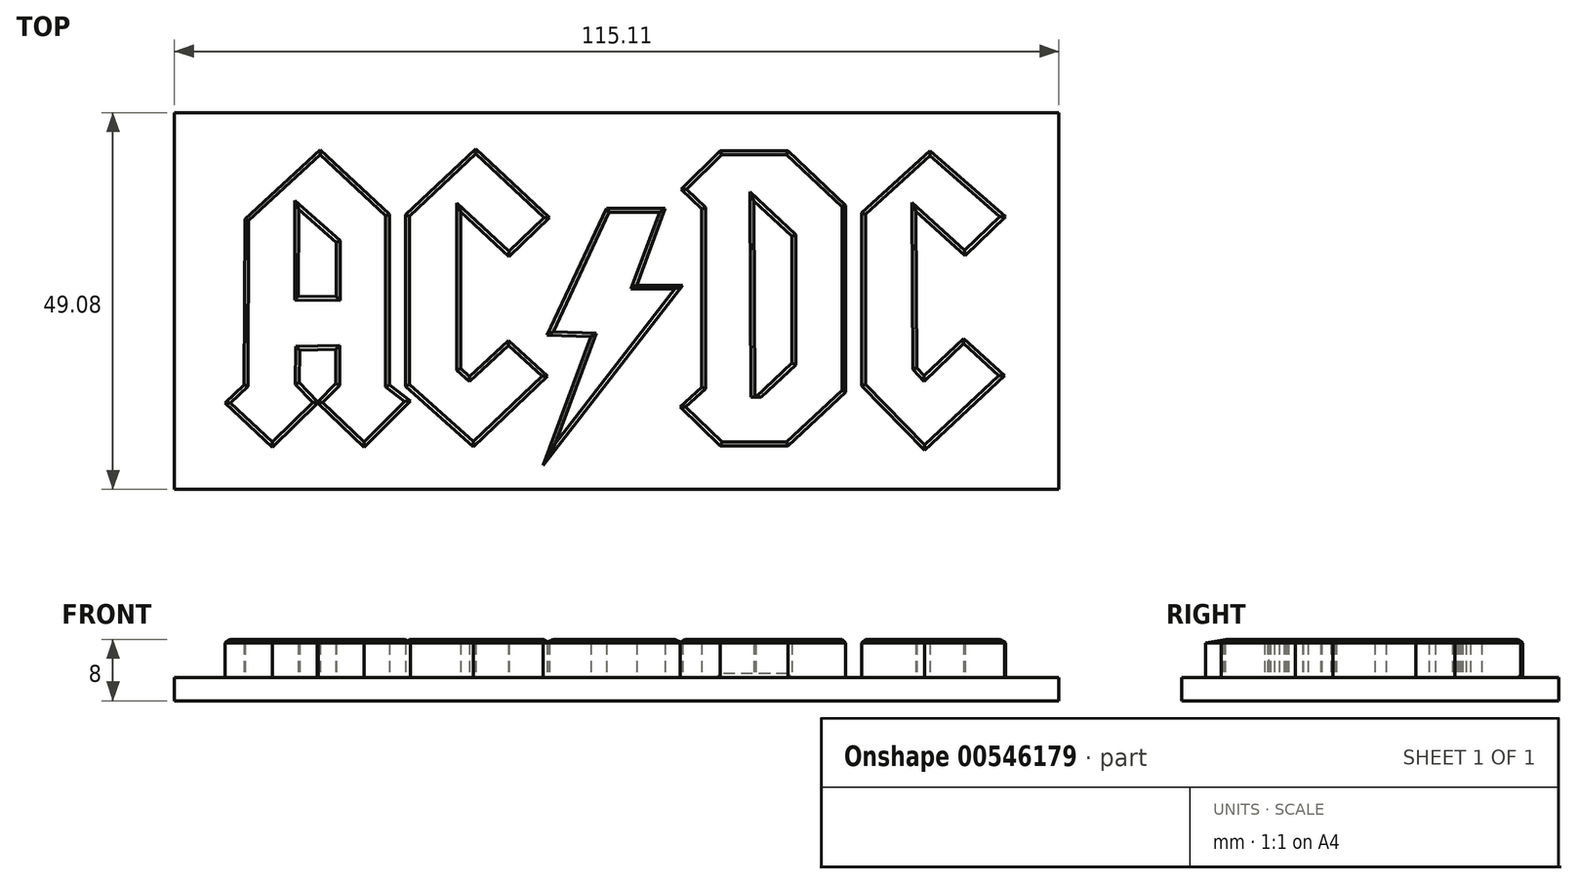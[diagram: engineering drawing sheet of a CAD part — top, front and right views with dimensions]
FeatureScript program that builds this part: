
annotation { "Feature Type Name" : "Feature", "Feature Type Description" : "" }
export const myFeature = defineFeature(function(context is Context, id is Id, definition is map)
    precondition{}
    {
        {
            var Q0;
            Q0=qCreatedBy(makeId("Top.planeOp"),FACE);
            var sketch = newSketch(context, id + "F0", { "sketchPlane" : qUnion([Q0])});
            skLineSegment(sketch, "E0", {"start": v(-47.24, 13.54) * mm, "end": v(-37.43, 22.56) * mm});
            skLineSegment(sketch, "E1", {"start": v(-37.43, 22.56) * mm, "end": v(-28.4, 14.16) * mm});
            skLineSegment(sketch, "E2", {"start": v(-28.4, 14.16) * mm, "end": v(-28.4, -8.08) * mm});
            skLineSegment(sketch, "E3", {"start": v(-49.82, -10.4) * mm, "end": v(-47.34, -8.08) * mm});
            skLineSegment(sketch, "E4", {"start": v(-47.34, -8.08) * mm, "end": v(-47.24, 13.54) * mm});
            skLineSegment(sketch, "E5", {"start": v(-40.2, 14.8) * mm, "end": v(-40.26, 3.45) * mm});
            skLineSegment(sketch, "E6", {"start": v(-40.26, 3.45) * mm, "end": v(-35.34, 3.43) * mm});
            skLineSegment(sketch, "E7", {"start": v(-35.34, 3.43) * mm, "end": v(-35.34, 10.49) * mm});
            skLineSegment(sketch, "E8", {"start": v(-35.34, 10.49) * mm, "end": v(-40.2, 14.8) * mm});
            skLineSegment(sketch, "E9", {"start": v(-40.1, -3.57) * mm, "end": v(-35.37, -3.46) * mm});
            skLineSegment(sketch, "E10", {"start": v(-35.37, -3.46) * mm, "end": v(-35.37, -7.9) * mm});
            skLineSegment(sketch, "E11", {"start": v(-40.18, -7.78) * mm, "end": v(-37.8, -10.25) * mm});
            skLineSegment(sketch, "E12", {"start": v(-40.18, -7.78) * mm, "end": v(-40.1, -3.57) * mm});
            skLineSegment(sketch, "E13", {"start": v(-28.4, -8.08) * mm, "end": v(-25.7, -10.15) * mm});
            skLineSegment(sketch, "E14", {"start": v(-25.7, -10.15) * mm, "end": v(-31.7, -16.22) * mm});
            skLineSegment(sketch, "E15", {"start": v(-31.7, -16.22) * mm, "end": v(-37.7, -10.5) * mm});
            skLineSegment(sketch, "E16", {"start": v(-37.7, -10.5) * mm, "end": v(-37.63, -10.41) * mm});
            skLineSegment(sketch, "E17", {"start": v(-37.63, -10.41) * mm, "end": v(-37.72, -10.28) * mm});
            skLineSegment(sketch, "E18", {"start": v(-37.72, -10.28) * mm, "end": v(-35.37, -7.9) * mm});
            skLineSegment(sketch, "E19", {"start": v(-37.8, -10.25) * mm, "end": v(-37.89, -10.38) * mm});
            skLineSegment(sketch, "E20", {"start": v(-37.89, -10.38) * mm, "end": v(-37.8, -10.5) * mm});
            skLineSegment(sketch, "E21", {"start": v(-37.8, -10.5) * mm, "end": v(-43.67, -16.18) * mm});
            skLineSegment(sketch, "E22", {"start": v(-43.67, -16.18) * mm, "end": v(-49.82, -10.4) * mm});
            skLineSegment(sketch, "E23", {"start": v(-12.87, 8.66) * mm, "end": v(-7.58, 13.71) * mm});
            skLineSegment(sketch, "E24", {"start": v(-7.58, 13.71) * mm, "end": v(-17.16, 22.69) * mm});
            skLineSegment(sketch, "E25", {"start": v(-17.16, 22.69) * mm, "end": v(-26.3, 14.11) * mm});
            skLineSegment(sketch, "E26", {"start": v(-26.3, 14.11) * mm, "end": v(-26.3, -8.25) * mm});
            skLineSegment(sketch, "E27", {"start": v(-26.3, -8.25) * mm, "end": v(-17.48, -16.14) * mm});
            skLineSegment(sketch, "E28", {"start": v(-17.48, -16.14) * mm, "end": v(-7.82, -6.93) * mm});
            skLineSegment(sketch, "E29", {"start": v(-7.82, -6.93) * mm, "end": v(-12.9, -2.28) * mm});
            skLineSegment(sketch, "E30", {"start": v(-12.9, -2.28) * mm, "end": v(-17.99, -6.96) * mm});
            skLineSegment(sketch, "E31", {"start": v(-17.99, -6.96) * mm, "end": v(-19.16, -5.93) * mm});
            skLineSegment(sketch, "E32", {"start": v(-19.16, -5.93) * mm, "end": v(-19.16, 14.47) * mm});
            skLineSegment(sketch, "E33", {"start": v(-19.16, 14.47) * mm, "end": v(-12.87, 8.66) * mm});
            skLineSegment(sketch, "E34", {"start": v(7.47, 14.9) * mm, "end": v(-0.15, 14.9) * mm});
            skLineSegment(sketch, "E35", {"start": v(-0.15, 14.9) * mm, "end": v(-7.88, -1.6) * mm});
            skLineSegment(sketch, "E36", {"start": v(-7.88, -1.6) * mm, "end": v(-2.18, -1.81) * mm});
            skLineSegment(sketch, "E37", {"start": v(-2.18, -1.81) * mm, "end": v(-8.4, -18.57) * mm});
            skLineSegment(sketch, "E38", {"start": v(-8.4, -18.57) * mm, "end": v(9.75, 4.9) * mm});
            skLineSegment(sketch, "E39", {"start": v(9.75, 4.9) * mm, "end": v(3.77, 4.9) * mm});
            skLineSegment(sketch, "E40", {"start": v(3.77, 4.9) * mm, "end": v(7.47, 14.9) * mm});
            skLineSegment(sketch, "E41", {"start": v(14.62, 22.43) * mm, "end": v(23.45, 22.43) * mm});
            skLineSegment(sketch, "E42", {"start": v(23.45, 22.43) * mm, "end": v(30.98, 15.31) * mm});
            skLineSegment(sketch, "E43", {"start": v(30.98, 15.31) * mm, "end": v(30.98, -9) * mm});
            skLineSegment(sketch, "E44", {"start": v(30.98, -9) * mm, "end": v(23.45, -16.03) * mm});
            skLineSegment(sketch, "E45", {"start": v(23.45, -16.03) * mm, "end": v(14.67, -16.03) * mm});
            skLineSegment(sketch, "E46", {"start": v(14.67, -16.03) * mm, "end": v(9.4, -10.93) * mm});
            skLineSegment(sketch, "E47", {"start": v(9.4, -10.93) * mm, "end": v(12.21, -8.37) * mm});
            skLineSegment(sketch, "E48", {"start": v(12.21, -8.37) * mm, "end": v(12.21, 14.84) * mm});
            skLineSegment(sketch, "E49", {"start": v(12.21, 14.84) * mm, "end": v(9.53, 17.37) * mm});
            skLineSegment(sketch, "E50", {"start": v(9.53, 17.37) * mm, "end": v(14.62, 22.43) * mm});
            skLineSegment(sketch, "E51", {"start": v(19.04, 15.9) * mm, "end": v(23.97, 11.3) * mm});
            skLineSegment(sketch, "E52", {"start": v(23.97, 11.3) * mm, "end": v(23.97, -5.23) * mm});
            skLineSegment(sketch, "E53", {"start": v(23.97, -5.23) * mm, "end": v(19.25, -9.66) * mm});
            skLineSegment(sketch, "E54", {"start": v(19.25, -9.66) * mm, "end": v(19.16, -9.66) * mm});
            skLineSegment(sketch, "E55", {"start": v(19.16, -9.66) * mm, "end": v(19.04, 15.9) * mm});
            skLineSegment(sketch, "E56", {"start": v(51.77, 13.84) * mm, "end": v(41.96, 22.43) * mm});
            skLineSegment(sketch, "E57", {"start": v(41.96, 22.43) * mm, "end": v(33.05, 14.35) * mm});
            skLineSegment(sketch, "E58", {"start": v(33.05, 14.35) * mm, "end": v(33.05, -8.2) * mm});
            skLineSegment(sketch, "E59", {"start": v(33.05, -8.2) * mm, "end": v(41.26, -16.56) * mm});
            skLineSegment(sketch, "E60", {"start": v(41.26, -16.56) * mm, "end": v(51.64, -6.9) * mm});
            skLineSegment(sketch, "E61", {"start": v(51.64, -6.9) * mm, "end": v(46.32, -2.02) * mm});
            skLineSegment(sketch, "E62", {"start": v(46.32, -2.02) * mm, "end": v(41.17, -6.9) * mm});
            skLineSegment(sketch, "E63", {"start": v(41.17, -6.9) * mm, "end": v(40.2, -5.87) * mm});
            skLineSegment(sketch, "E64", {"start": v(40.2, -5.87) * mm, "end": v(40.1, 14.55) * mm});
            skLineSegment(sketch, "E65", {"start": v(40.1, 14.55) * mm, "end": v(46.5, 8.78) * mm});
            skLineSegment(sketch, "E66", {"start": v(46.5, 8.78) * mm, "end": v(51.77, 13.84) * mm});
            skSolve(sketch);
        }
        {
            var Q0;
            Q0 = qSketchRegion(id + "F0", true);
            extrude(context, id + "F1", {"entities" : qUnion([Q0]), "depth" : 5 * mm, "offsetDistance" : 25.4 * mm});
        }
        {
            var Q0;
            Q0=makeQuery(id+"F1.opExtrude","CAP_EDGE",EDGE,{"disambiguationData":[OSD([sQuery(id+"F0.wireOp",EDGE,"E25")])],"isStart":false});
            var Q1;
            Q1=makeQuery(id+"F1.opExtrude","CAP_EDGE",EDGE,{"disambiguationData":[OSD([sQuery(id+"F0.wireOp",EDGE,"E24")])],"isStart":false});
            var Q2;
            Q2=makeQuery(id+"F1.opExtrude","CAP_EDGE",EDGE,{"disambiguationData":[OSD([sQuery(id+"F0.wireOp",EDGE,"E23")])],"isStart":false});
            var Q3;
            Q3=makeQuery(id+"F1.opExtrude","CAP_EDGE",EDGE,{"disambiguationData":[OSD([sQuery(id+"F0.wireOp",EDGE,"E33")])],"isStart":false});
            var Q4;
            Q4=makeQuery(id+"F1.opExtrude","CAP_EDGE",EDGE,{"disambiguationData":[OSD([sQuery(id+"F0.wireOp",EDGE,"E32")])],"isStart":false});
            var Q5;
            Q5=makeQuery(id+"F1.opExtrude","CAP_EDGE",EDGE,{"disambiguationData":[OSD([sQuery(id+"F0.wireOp",EDGE,"E31")])],"isStart":false});
            var Q6;
            Q6=makeQuery(id+"F1.opExtrude","CAP_EDGE",EDGE,{"disambiguationData":[OSD([sQuery(id+"F0.wireOp",EDGE,"E30")])],"isStart":false});
            var Q7;
            Q7=makeQuery(id+"F1.opExtrude","CAP_EDGE",EDGE,{"disambiguationData":[OSD([sQuery(id+"F0.wireOp",EDGE,"E29")])],"isStart":false});
            var Q8;
            Q8=makeQuery(id+"F1.opExtrude","CAP_EDGE",EDGE,{"disambiguationData":[OSD([sQuery(id+"F0.wireOp",EDGE,"E28")])],"isStart":false});
            var Q9;
            Q9=makeQuery(id+"F1.opExtrude","CAP_EDGE",EDGE,{"disambiguationData":[OSD([sQuery(id+"F0.wireOp",EDGE,"E27")])],"isStart":false});
            var Q10;
            Q10=makeQuery(id+"F1.opExtrude","CAP_EDGE",EDGE,{"disambiguationData":[OSD([sQuery(id+"F0.wireOp",EDGE,"E26")])],"isStart":false});
            chamfer(context, id + "F2", {"entities" : qUnion([Q0, Q1, Q2, Q3, Q4, Q5, Q6, Q7, Q8, Q9, Q10]), "width" : 0.5 * mm, "tangentPropagation" : true});
        }
        {
            var Q0;
            Q0=makeQuery(id+"F1.opExtrude","CAP_EDGE",EDGE,{"disambiguationData":[OSD([sQuery(id+"F0.wireOp",EDGE,"E0")])],"isStart":false});
            var Q1;
            Q1=makeQuery(id+"F1.opExtrude","CAP_EDGE",EDGE,{"disambiguationData":[OSD([sQuery(id+"F0.wireOp",EDGE,"E1")])],"isStart":false});
            var Q2;
            Q2=makeQuery(id+"F1.opExtrude","CAP_EDGE",EDGE,{"disambiguationData":[OSD([sQuery(id+"F0.wireOp",EDGE,"E2")])],"isStart":false});
            var Q3;
            Q3=makeQuery(id+"F1.opExtrude","CAP_EDGE",EDGE,{"disambiguationData":[OSD([sQuery(id+"F0.wireOp",EDGE,"E13")])],"isStart":false});
            var Q4;
            Q4=makeQuery(id+"F1.opExtrude","CAP_EDGE",EDGE,{"disambiguationData":[OSD([sQuery(id+"F0.wireOp",EDGE,"E14")])],"isStart":false});
            var Q5;
            Q5=makeQuery(id+"F1.opExtrude","CAP_EDGE",EDGE,{"disambiguationData":[OSD([sQuery(id+"F0.wireOp",EDGE,"E15")])],"isStart":false});
            var Q6;
            Q6=makeQuery(id+"F1.opExtrude","CAP_EDGE",EDGE,{"disambiguationData":[OSD([sQuery(id+"F0.wireOp",EDGE,"E4")])],"isStart":false});
            var Q7;
            Q7=makeQuery(id+"F1.opExtrude","CAP_EDGE",EDGE,{"disambiguationData":[OSD([sQuery(id+"F0.wireOp",EDGE,"E3")])],"isStart":false});
            var Q8;
            Q8=makeQuery(id+"F1.opExtrude","CAP_EDGE",EDGE,{"disambiguationData":[OSD([sQuery(id+"F0.wireOp",EDGE,"E22")])],"isStart":false});
            var Q9;
            Q9=makeQuery(id+"F1.opExtrude","CAP_EDGE",EDGE,{"disambiguationData":[OSD([sQuery(id+"F0.wireOp",EDGE,"E21")])],"isStart":false});
            var Q10;
            Q10=makeQuery(id+"F1.opExtrude","CAP_EDGE",EDGE,{"disambiguationData":[OSD([sQuery(id+"F0.wireOp",EDGE,"E11")])],"isStart":false});
            var Q11;
            Q11=makeQuery(id+"F1.opExtrude","CAP_EDGE",EDGE,{"disambiguationData":[OSD([sQuery(id+"F0.wireOp",EDGE,"E12")])],"isStart":false});
            var Q12;
            Q12=makeQuery(id+"F1.opExtrude","CAP_EDGE",EDGE,{"disambiguationData":[OSD([sQuery(id+"F0.wireOp",EDGE,"E9")])],"isStart":false});
            var Q13;
            Q13=makeQuery(id+"F1.opExtrude","CAP_EDGE",EDGE,{"disambiguationData":[OSD([sQuery(id+"F0.wireOp",EDGE,"E10")])],"isStart":false});
            var Q14;
            Q14=makeQuery(id+"F1.opExtrude","CAP_EDGE",EDGE,{"disambiguationData":[OSD([sQuery(id+"F0.wireOp",EDGE,"E18")])],"isStart":false});
            var Q15;
            Q15=makeQuery(id+"F1.opExtrude","CAP_EDGE",EDGE,{"disambiguationData":[OSD([sQuery(id+"F0.wireOp",EDGE,"E7")])],"isStart":false});
            var Q16;
            Q16=makeQuery(id+"F1.opExtrude","CAP_EDGE",EDGE,{"disambiguationData":[OSD([sQuery(id+"F0.wireOp",EDGE,"E8")])],"isStart":false});
            var Q17;
            Q17=makeQuery(id+"F1.opExtrude","CAP_EDGE",EDGE,{"disambiguationData":[OSD([sQuery(id+"F0.wireOp",EDGE,"E5")])],"isStart":false});
            var Q18;
            Q18=makeQuery(id+"F1.opExtrude","CAP_EDGE",EDGE,{"disambiguationData":[OSD([sQuery(id+"F0.wireOp",EDGE,"E6")])],"isStart":false});
            chamfer(context, id + "F3", {"entities" : qUnion([Q0, Q1, Q2, Q3, Q4, Q5, Q6, Q7, Q8, Q9, Q10, Q11, Q12, Q13, Q14, Q15, Q16, Q17, Q18]), "width" : 0.5 * mm, "tangentPropagation" : true});
        }
        {
            var Q0;
            Q0=makeQuery(id+"F1.opExtrude","CAP_EDGE",EDGE,{"disambiguationData":[OSD([sQuery(id+"F0.wireOp",EDGE,"E35")])],"isStart":false});
            var Q1;
            Q1=makeQuery(id+"F1.opExtrude","CAP_EDGE",EDGE,{"disambiguationData":[OSD([sQuery(id+"F0.wireOp",EDGE,"E39")])],"isStart":false});
            var Q2;
            Q2=makeQuery(id+"F1.opExtrude","CAP_EDGE",EDGE,{"disambiguationData":[OSD([sQuery(id+"F0.wireOp",EDGE,"E38")])],"isStart":false});
            var Q3;
            Q3=makeQuery(id+"F1.opExtrude","CAP_EDGE",EDGE,{"disambiguationData":[OSD([sQuery(id+"F0.wireOp",EDGE,"E37")])],"isStart":false});
            var Q4;
            Q4=makeQuery(id+"F1.opExtrude","CAP_EDGE",EDGE,{"disambiguationData":[OSD([sQuery(id+"F0.wireOp",EDGE,"E36")])],"isStart":false});
            var Q5;
            Q5=makeQuery(id+"F1.opExtrude","CAP_EDGE",EDGE,{"disambiguationData":[OSD([sQuery(id+"F0.wireOp",EDGE,"E48")])],"isStart":false});
            var Q6;
            Q6=makeQuery(id+"F1.opExtrude","CAP_EDGE",EDGE,{"disambiguationData":[OSD([sQuery(id+"F0.wireOp",EDGE,"E49")])],"isStart":false});
            var Q7;
            Q7=makeQuery(id+"F1.opExtrude","CAP_EDGE",EDGE,{"disambiguationData":[OSD([sQuery(id+"F0.wireOp",EDGE,"E50")])],"isStart":false});
            var Q8;
            Q8=makeQuery(id+"F1.opExtrude","CAP_EDGE",EDGE,{"disambiguationData":[OSD([sQuery(id+"F0.wireOp",EDGE,"E41")])],"isStart":true});
            var Q9;
            Q9=makeQuery(id+"F1.opExtrude","CAP_EDGE",EDGE,{"disambiguationData":[OSD([sQuery(id+"F0.wireOp",EDGE,"E42")])],"isStart":false});
            var Q10;
            Q10=makeQuery(id+"F1.opExtrude","CAP_EDGE",EDGE,{"disambiguationData":[OSD([sQuery(id+"F0.wireOp",EDGE,"E43")])],"isStart":false});
            var Q11;
            Q11=makeQuery(id+"F1.opExtrude","CAP_EDGE",EDGE,{"disambiguationData":[OSD([sQuery(id+"F0.wireOp",EDGE,"E44")])],"isStart":false});
            var Q12;
            Q12=makeQuery(id+"F1.opExtrude","CAP_EDGE",EDGE,{"disambiguationData":[OSD([sQuery(id+"F0.wireOp",EDGE,"E45")])],"isStart":false});
            var Q13;
            Q13=makeQuery(id+"F1.opExtrude","CAP_EDGE",EDGE,{"disambiguationData":[OSD([sQuery(id+"F0.wireOp",EDGE,"E46")])],"isStart":false});
            var Q14;
            Q14=makeQuery(id+"F1.opExtrude","CAP_EDGE",EDGE,{"disambiguationData":[OSD([sQuery(id+"F0.wireOp",EDGE,"E55")])],"isStart":false});
            var Q15;
            Q15=makeQuery(id+"F1.opExtrude","CAP_EDGE",EDGE,{"disambiguationData":[OSD([sQuery(id+"F0.wireOp",EDGE,"E53")])],"isStart":false});
            var Q16;
            Q16=makeQuery(id+"F1.opExtrude","CAP_EDGE",EDGE,{"disambiguationData":[OSD([sQuery(id+"F0.wireOp",EDGE,"E52")])],"isStart":false});
            var Q17;
            Q17=makeQuery(id+"F1.opExtrude","CAP_EDGE",EDGE,{"disambiguationData":[OSD([sQuery(id+"F0.wireOp",EDGE,"E51")])],"isStart":false});
            var Q18;
            Q18=makeQuery(id+"F1.opExtrude","CAP_EDGE",EDGE,{"disambiguationData":[OSD([sQuery(id+"F0.wireOp",EDGE,"E58")])],"isStart":false});
            var Q19;
            Q19=makeQuery(id+"F1.opExtrude","CAP_EDGE",EDGE,{"disambiguationData":[OSD([sQuery(id+"F0.wireOp",EDGE,"E57")])],"isStart":false});
            var Q20;
            Q20=makeQuery(id+"F1.opExtrude","CAP_EDGE",EDGE,{"disambiguationData":[OSD([sQuery(id+"F0.wireOp",EDGE,"E56")])],"isStart":false});
            var Q21;
            Q21=makeQuery(id+"F1.opExtrude","CAP_EDGE",EDGE,{"disambiguationData":[OSD([sQuery(id+"F0.wireOp",EDGE,"E66")])],"isStart":false});
            var Q22;
            Q22=makeQuery(id+"F1.opExtrude","CAP_EDGE",EDGE,{"disambiguationData":[OSD([sQuery(id+"F0.wireOp",EDGE,"E65")])],"isStart":false});
            var Q23;
            Q23=makeQuery(id+"F1.opExtrude","CAP_EDGE",EDGE,{"disambiguationData":[OSD([sQuery(id+"F0.wireOp",EDGE,"E64")])],"isStart":false});
            var Q24;
            Q24=makeQuery(id+"F1.opExtrude","CAP_EDGE",EDGE,{"disambiguationData":[OSD([sQuery(id+"F0.wireOp",EDGE,"E63")])],"isStart":false});
            var Q25;
            Q25=makeQuery(id+"F1.opExtrude","CAP_EDGE",EDGE,{"disambiguationData":[OSD([sQuery(id+"F0.wireOp",EDGE,"E62")])],"isStart":false});
            var Q26;
            Q26=makeQuery(id+"F1.opExtrude","CAP_EDGE",EDGE,{"disambiguationData":[OSD([sQuery(id+"F0.wireOp",EDGE,"E61")])],"isStart":false});
            var Q27;
            Q27=makeQuery(id+"F1.opExtrude","CAP_EDGE",EDGE,{"disambiguationData":[OSD([sQuery(id+"F0.wireOp",EDGE,"E60")])],"isStart":false});
            var Q28;
            Q28=makeQuery(id+"F1.opExtrude","CAP_EDGE",EDGE,{"disambiguationData":[OSD([sQuery(id+"F0.wireOp",EDGE,"E59")])],"isStart":false});
            var Q29;
            Q29=makeQuery(id+"F1.opExtrude","CAP_EDGE",EDGE,{"disambiguationData":[OSD([sQuery(id+"F0.wireOp",EDGE,"E40")])],"isStart":false});
            var Q30;
            Q30=makeQuery(id+"F1.opExtrude","CAP_EDGE",EDGE,{"disambiguationData":[OSD([sQuery(id+"F0.wireOp",EDGE,"E34")])],"isStart":false});
            var Q31;
            Q31=makeQuery(id+"F1.opExtrude","CAP_EDGE",EDGE,{"disambiguationData":[OSD([sQuery(id+"F0.wireOp",EDGE,"E41")])],"isStart":false});
            var Q32;
            Q32=makeQuery(id+"F1.opExtrude","CAP_EDGE",EDGE,{"disambiguationData":[OSD([sQuery(id+"F0.wireOp",EDGE,"E47")])],"isStart":false});
            chamfer(context, id + "F4", {"entities" : qUnion([Q0, Q1, Q2, Q3, Q4, Q5, Q6, Q7, Q8, Q9, Q10, Q11, Q12, Q13, Q14, Q15, Q16, Q17, Q18, Q19, Q20, Q21, Q22, Q23, Q24, Q25, Q26, Q27, Q28, Q29, Q30, Q31, Q32]), "width" : 0.5 * mm, "tangentPropagation" : true});
        }
        {
            var Q0;
            Q0=qCreatedBy(makeId("Top.planeOp"),FACE);
            var sketch = newSketch(context, id + "F5", { "sketchPlane" : qUnion([Q0])});
            skLineSegment(sketch, "E67.bottom", {"start": v(-56.39, 27.39) * mm, "end": v(58.72, 27.39) * mm});
            skLineSegment(sketch, "E67.top", {"start": v(-56.39, -21.69) * mm, "end": v(58.72, -21.69) * mm});
            skLineSegment(sketch, "E67.left", {"start": v(-56.39, 27.39) * mm, "end": v(-56.39, -21.69) * mm});
            skLineSegment(sketch, "E67.right", {"start": v(58.72, 27.39) * mm, "end": v(58.72, -21.69) * mm});
            skLineSegment(sketch, "E68", {"start": v(-37.44, 22.56) * mm, "end": v(-56.39, 22.56) * mm, "construction": true});
            skSolve(sketch);
        }
        {
            var Q0;
            Q0=makeQuery(id+"F5.imprint","IMPRINT",FACE,{"disambiguationData":[TD([[makeQuery(id+"F5.imprint","IMPRINT",EDGE,{"derivedFrom":sQuery(id+"F5.wireOp",EDGE,"E67.bottom")}),-1.0]])]});
            extrude(context, id + "F6", {"entities" : qUnion([Q0]), "oppositeDirection" : true, "depth" : 3 * mm, "offsetDistance" : 25 * mm});
        }
    });
